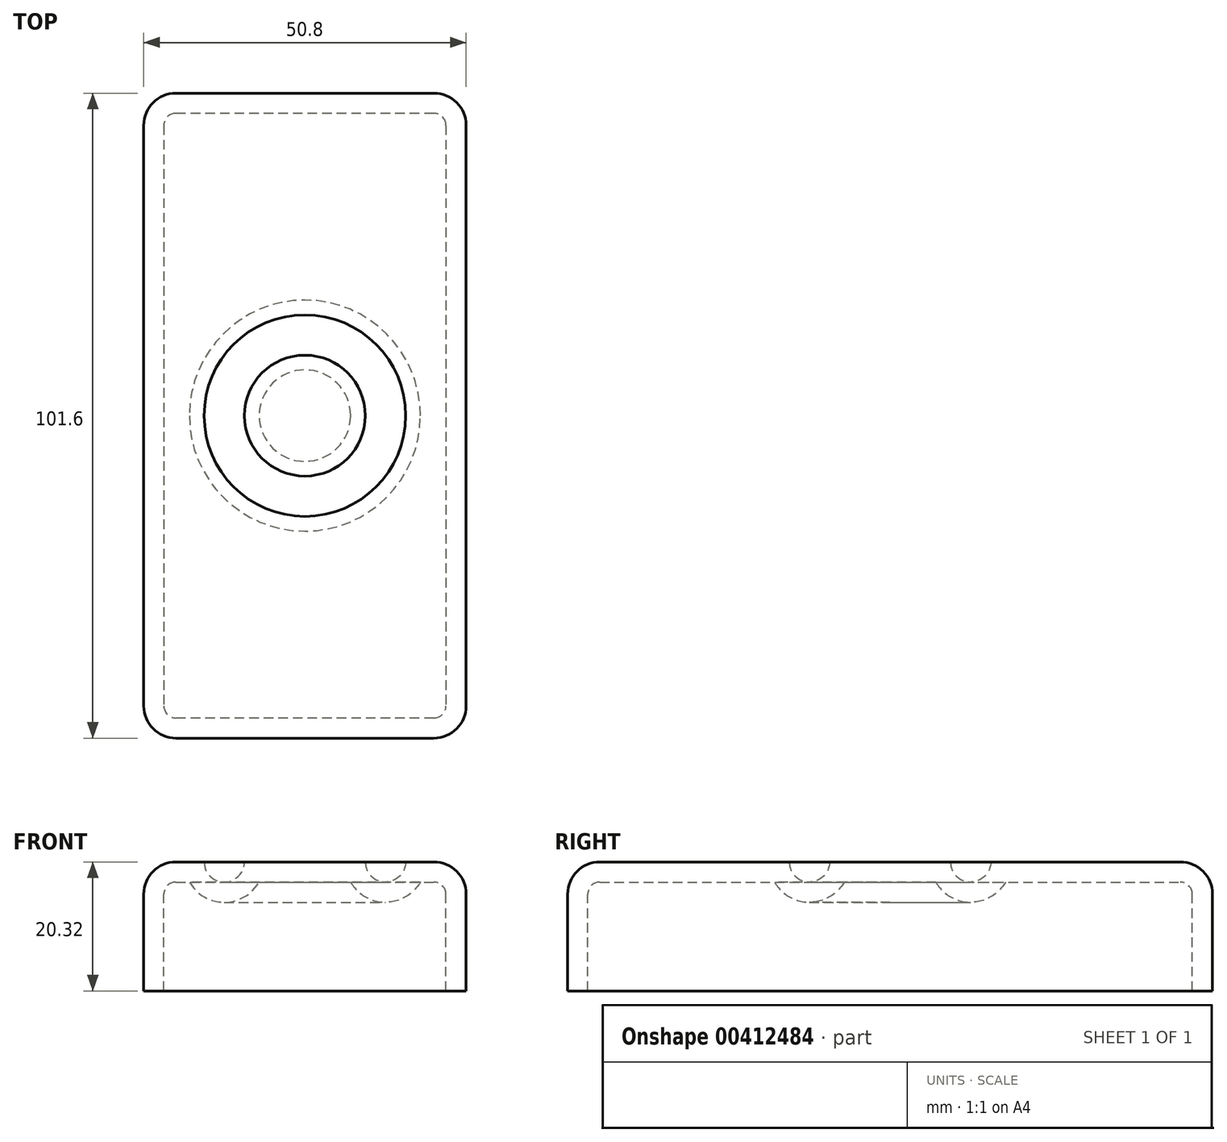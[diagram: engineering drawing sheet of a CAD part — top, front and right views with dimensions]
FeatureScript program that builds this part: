
annotation { "Feature Type Name" : "Feature", "Feature Type Description" : "" }
export const myFeature = defineFeature(function(context is Context, id is Id, definition is map)
    precondition{}
    {
        {
            var Q0;
            Q0=qCreatedBy(makeId("Top.planeOp"),FACE);
            var sketch = newSketch(context, id + "F0", { "sketchPlane" : qUnion([Q0])});
            skLineSegment(sketch, "E0.bottom", {"start": v(0, 0) * mm, "end": v(50.8, 0) * mm});
            skLineSegment(sketch, "E0.top", {"start": v(0, 101.6) * mm, "end": v(50.8, 101.6) * mm});
            skLineSegment(sketch, "E0.left", {"start": v(0, 0) * mm, "end": v(0, 101.6) * mm});
            skLineSegment(sketch, "E0.right", {"start": v(50.8, 0) * mm, "end": v(50.8, 101.6) * mm});
            skSolve(sketch);
        }
        {
            var Q0;
            Q0=makeQuery(id+"F0.imprint","IMPRINT",FACE,{"disambiguationData":[TD([[makeQuery(id+"F0.imprint","IMPRINT",EDGE,{"derivedFrom":sQuery(id+"F0.wireOp",EDGE,"E0.bottom")}),1.0]])]});
            extrude(context, id + "F1", {"entities" : qUnion([Q0]), "depth" : 25.4 * mm});
        }
        {
            var Q0;
            Q0=makeQuery(id+"F1.opExtrude","SWEPT_FACE",FACE,{"disambiguationData":[OSD([sQuery(id+"F0.wireOp",EDGE,"E0.right")])]});
            var Q1;
            Q1=makeQuery(id+"F1.opExtrude","CAP_FACE",FACE,{"disambiguationData":[OSD([sQuery(id+"F0.wireOp",EDGE,"E0.bottom"),sQuery(id+"F0.wireOp",EDGE,"E0.top"),sQuery(id+"F0.wireOp",EDGE,"E0.left"),sQuery(id+"F0.wireOp",EDGE,"E0.right")])],"isStart":false});
            var Q2;
            Q2=makeQuery(id+"F1.opExtrude","SWEPT_FACE",FACE,{"disambiguationData":[OSD([sQuery(id+"F0.wireOp",EDGE,"E0.bottom")])]});
            var Q3;
            Q3=makeQuery(id+"F1.opExtrude","SWEPT_FACE",FACE,{"disambiguationData":[OSD([sQuery(id+"F0.wireOp",EDGE,"E0.top")])]});
            var Q4;
            Q4=makeQuery(id+"F1.opExtrude","SWEPT_FACE",FACE,{"disambiguationData":[OSD([sQuery(id+"F0.wireOp",EDGE,"E0.left")])]});
            fillet(context, id + "F2", {"entities" : qUnion([Q0, Q1, Q2, Q3, Q4]), "radius" : 5.08 * mm, "tangentPropagation" : true, "allowEdgeOverflow" : false});
        }
        {
            var Q0;
            Q0=makeQuery(id+"F1.opExtrude","SWEPT_FACE",FACE,{"disambiguationData":[OSD([sQuery(id+"F0.wireOp",EDGE,"E0.right")])]});
            var Q1;
            Q1=makeQuery(id+"F1.opExtrude","SWEPT_FACE",FACE,{"disambiguationData":[OSD([sQuery(id+"F0.wireOp",EDGE,"E0.left")])]});
            cPlane(context, id + "F3", {"entities" : qUnion([Q0, Q1]), "cplaneType" : CPlaneType.MID_PLANE, "offset" : 25.4 * mm, "width" : 152.4 * mm, "height" : 152.4 * mm});
        }
        {
            var Q0;
            Q0=qCreatedBy(id+"F3.planeOp",FACE);
            var sketch = newSketch(context, id + "F4", { "sketchPlane" : qUnion([Q0])});
            skCircle(sketch, "E1", {"center": v(63.5, 25.4) * mm, "radius": 3.18 * mm});
            skLineSegment(sketch, "E2", {"start": v(50.8, 25.4) * mm, "end": v(50.8, 0) * mm, "construction": true});
            skSolve(sketch);
        }
        {
            var Q0;
            Q0=makeQuery(id+"F4.imprint","IMPRINT",FACE,{"disambiguationData":[TD([[makeQuery(id+"F4.imprint","IMPRINT",EDGE,{"derivedFrom":sQuery(id+"F4.wireOp",EDGE,"E1")}),1.0]])]});
            var Q1;
            Q1=sQuery(id+"F4.wireOp",EDGE,"E2");
            revolve(context, id + "F5", {"operationType" : NewBodyOperationType.REMOVE, "entities" : qUnion([Q0]), "axis" : qUnion([Q1]), "revolveType" : RevolveType.FULL, "oppositeDirection" : true});
        }
        {
            var Q0;
            Q0=makeQuery(id+"F1.opExtrude","CAP_FACE",FACE,{"disambiguationData":[OSD([sQuery(id+"F0.wireOp",EDGE,"E0.bottom"),sQuery(id+"F0.wireOp",EDGE,"E0.top"),sQuery(id+"F0.wireOp",EDGE,"E0.left"),sQuery(id+"F0.wireOp",EDGE,"E0.right")])],"isStart":true});
            var Q1;
            {var subQ0=sQuery(id+"F0.wireOp",EDGE,"E0.left");Q1=makeQuery(id+"F2.opFillet","BLEND_FACE",FACE,{"disambiguationData":[OSD([subQ0]),TDD([makeQuery(id+"F1.opExtrude","CAP_EDGE",EDGE,{"disambiguationData":[OSD([subQ0])],"isStart":true})])]});}
            var Q2;
            {var subQ0=sQuery(id+"F0.wireOp",EDGE,"E0.left");var subQ1=sQuery(id+"F0.wireOp",EDGE,"E0.bottom");Q2=makeQuery(id+"F2.opFillet","BLEND_FACE",FACE,{"disambiguationData":[OSD([subQ1,subQ0]),TDD([makeQuery(id+"F1.opExtrude","CAP_VERTEX",VERTEX,{"disambiguationData":[OSD([subQ1,subQ0])],"isStart":true})])]});}
            var Q3;
            {var subQ0=sQuery(id+"F0.wireOp",EDGE,"E0.bottom");Q3=makeQuery(id+"F2.opFillet","BLEND_FACE",FACE,{"disambiguationData":[OSD([subQ0]),TDD([makeQuery(id+"F1.opExtrude","CAP_EDGE",EDGE,{"disambiguationData":[OSD([subQ0])],"isStart":true})])]});}
            var Q4;
            {var subQ0=sQuery(id+"F0.wireOp",EDGE,"E0.right");var subQ1=sQuery(id+"F0.wireOp",EDGE,"E0.bottom");Q4=makeQuery(id+"F2.opFillet","BLEND_FACE",FACE,{"disambiguationData":[OSD([subQ1,subQ0]),TDD([makeQuery(id+"F1.opExtrude","CAP_VERTEX",VERTEX,{"disambiguationData":[OSD([subQ1,subQ0])],"isStart":true})])]});}
            var Q5;
            {var subQ0=sQuery(id+"F0.wireOp",EDGE,"E0.right");Q5=makeQuery(id+"F2.opFillet","BLEND_FACE",FACE,{"disambiguationData":[OSD([subQ0]),TDD([makeQuery(id+"F1.opExtrude","CAP_EDGE",EDGE,{"disambiguationData":[OSD([subQ0])],"isStart":true})])]});}
            var Q6;
            {var subQ0=sQuery(id+"F0.wireOp",EDGE,"E0.left");var subQ1=sQuery(id+"F0.wireOp",EDGE,"E0.top");Q6=makeQuery(id+"F2.opFillet","BLEND_FACE",FACE,{"disambiguationData":[OSD([subQ1,subQ0]),TDD([makeQuery(id+"F1.opExtrude","CAP_VERTEX",VERTEX,{"disambiguationData":[OSD([subQ1,subQ0])],"isStart":true})])]});}
            var Q7;
            {var subQ0=sQuery(id+"F0.wireOp",EDGE,"E0.top");Q7=makeQuery(id+"F2.opFillet","BLEND_FACE",FACE,{"disambiguationData":[OSD([subQ0]),TDD([makeQuery(id+"F1.opExtrude","CAP_EDGE",EDGE,{"disambiguationData":[OSD([subQ0])],"isStart":true})])]});}
            var Q8;
            {var subQ0=sQuery(id+"F0.wireOp",EDGE,"E0.right");var subQ1=sQuery(id+"F0.wireOp",EDGE,"E0.top");Q8=makeQuery(id+"F2.opFillet","BLEND_FACE",FACE,{"disambiguationData":[OSD([subQ1,subQ0]),TDD([makeQuery(id+"F1.opExtrude","CAP_VERTEX",VERTEX,{"disambiguationData":[OSD([subQ1,subQ0])],"isStart":true})])]});}
            shell(context, id + "F6", {"entities" : qUnion([Q0, Q1, Q2, Q3, Q4, Q5, Q6, Q7, Q8]), "thickness" : 3.17 * mm});
        }
    });
